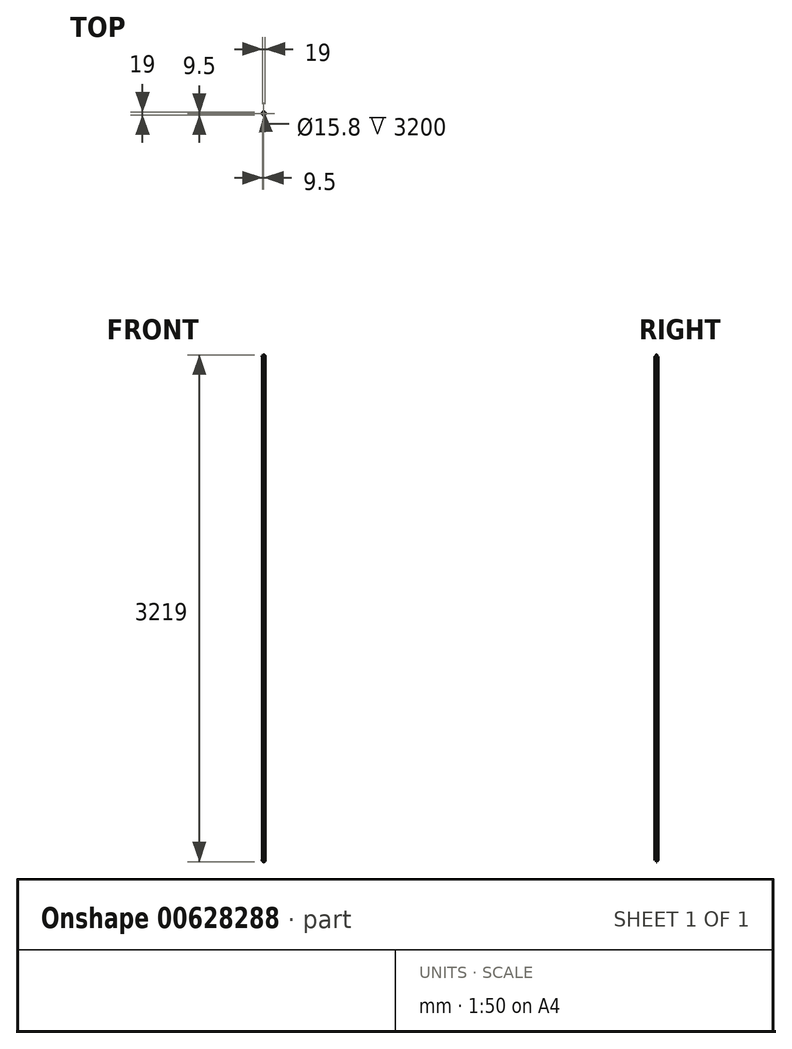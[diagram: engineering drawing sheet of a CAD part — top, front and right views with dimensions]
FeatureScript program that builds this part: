
annotation { "Feature Type Name" : "Feature", "Feature Type Description" : "" }
export const myFeature = defineFeature(function(context is Context, id is Id, definition is map)
    precondition{}
    {
        {
            var Q0;
            Q0=qCreatedBy(makeId("Top.planeOp"),FACE);
            var sketch = newSketch(context, id + "F0", { "sketchPlane" : qUnion([Q0])});
            skCircle(sketch, "E0", {"center": v(0, 0) * mm, "radius": 9.5 * mm});
            skCircle(sketch, "E1", {"center": v(0, 0) * mm, "radius": 7.9 * mm});
            skSolve(sketch);
        }
        {
            var Q0;
            Q0=makeQuery(id+"F0.imprint","IMPRINT",FACE,{"disambiguationData":[TD([[makeQuery(id+"F0.imprint","IMPRINT",EDGE,{"derivedFrom":sQuery(id+"F0.wireOp",EDGE,"E0")}),1.0]])]});
            extrude(context, id + "F1", {"entities" : qUnion([Q0]), "depth" : 1600 * mm, "offsetDistance" : 25 * mm});
        }
        {
            var Q0;
            Q0=qCreatedBy(makeId("Front.planeOp"),FACE);
            var sketch = newSketch(context, id + "F2", { "sketchPlane" : qUnion([Q0])});
            skCircle(sketch, "E2", {"center": v(0, 0) * mm, "radius": 9.5 * mm});
            skSolve(sketch);
        }
        {
            var Q0;
            Q0 = qSketchRegion(id + "F2", true);
            extrude(context, id + "F3", {"entities" : qUnion([Q0]), "operationType" : NewBodyOperationType.ADD, "depth" : 1.6 * mm, "offsetDistance" : 25 * mm});
        }
        {
            var Q0;
            Q0=makeQuery(id+"F3.opExtrude","CAP_FACE",FACE,{"disambiguationData":[OSD([sQuery(id+"F2.wireOp",EDGE,"E2")])],"isStart":true});
            extrude(context, id + "F4", {"entities" : qUnion([Q0]), "operationType" : NewBodyOperationType.ADD, "depth" : 1.6 * mm, "offsetDistance" : 25 * mm});
        }
        {
            var Q0;
            Q0=makeQuery(id+"F1.opExtrude","SWEPT_BODY",BODY,{"disambiguationData":[OSD([sQuery(id+"F0.wireOp",EDGE,"E0"),sQuery(id+"F0.wireOp",EDGE,"E1")])]});
            var Q1;
            Q1=makeQuery(id+"F1.opExtrude","CAP_FACE",FACE,{"disambiguationData":[OSD([sQuery(id+"F0.wireOp",EDGE,"E0"),sQuery(id+"F0.wireOp",EDGE,"E1")])],"isStart":false});
            mirror(context, id + "F5", {"operationType" : NewBodyOperationType.ADD, "entities" : qUnion([Q0]), "mirrorPlane" : qUnion([Q1])});
        }
    });
